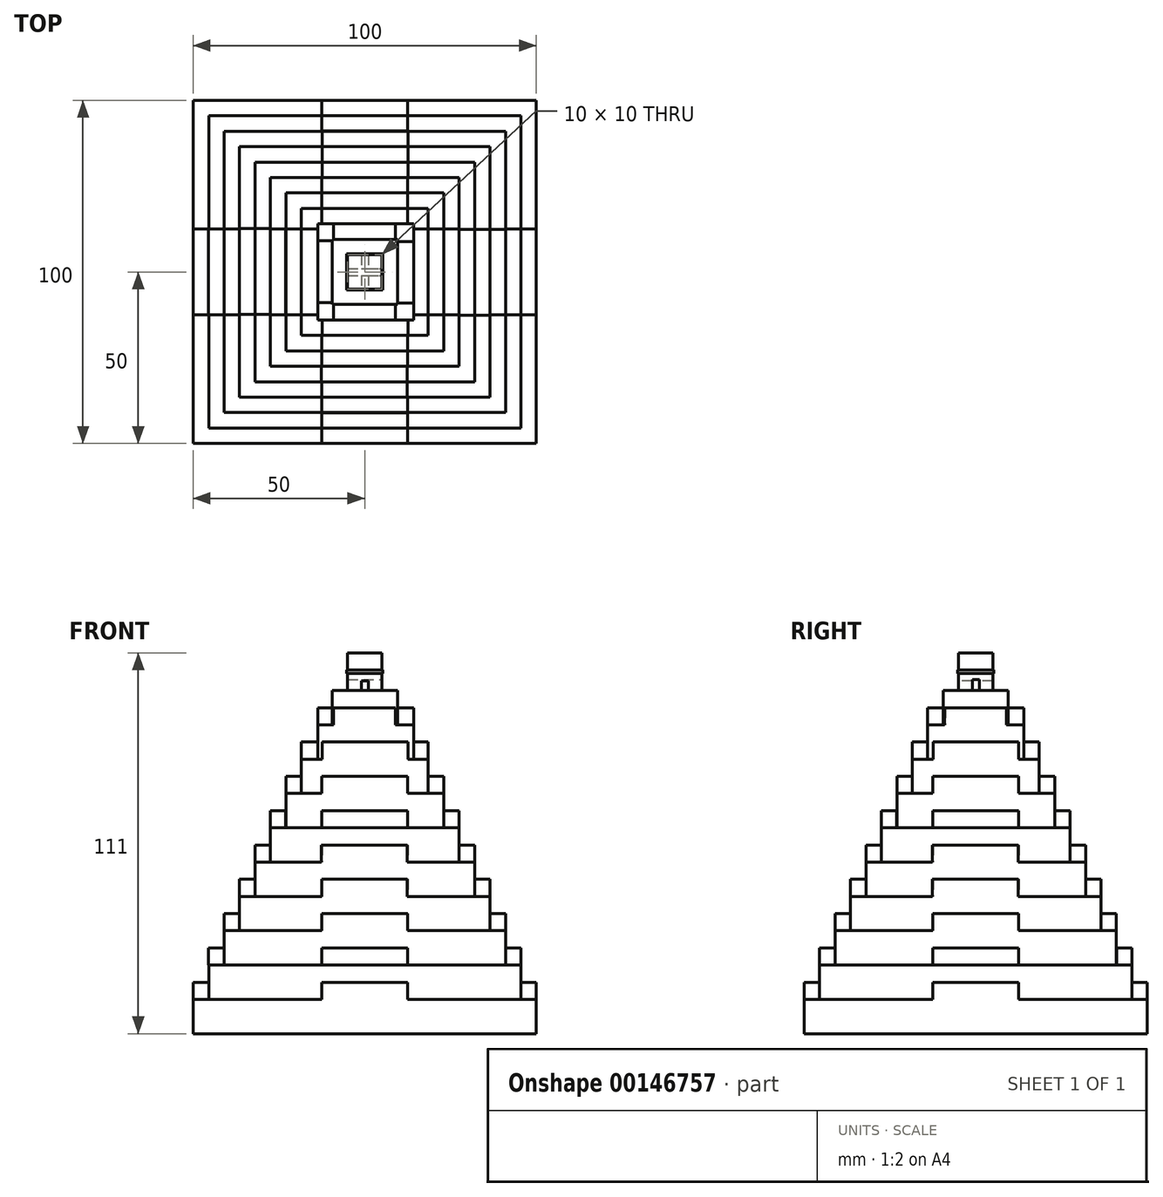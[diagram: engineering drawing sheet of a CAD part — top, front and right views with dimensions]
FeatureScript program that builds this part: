
annotation { "Feature Type Name" : "Feature", "Feature Type Description" : "" }
export const myFeature = defineFeature(function(context is Context, id is Id, definition is map)
    precondition{}
    {
        {
            var Q0;
            Q0=qCreatedBy(makeId("Top.planeOp"),FACE);
            var sketch = newSketch(context, id + "F0", { "sketchPlane" : qUnion([Q0])});
            skLineSegment(sketch, "E0.bottom", {"start": v(-50, 50) * mm, "end": v(50, 50) * mm});
            skLineSegment(sketch, "E0.top", {"start": v(-50, -50) * mm, "end": v(50, -50) * mm});
            skLineSegment(sketch, "E0.left", {"start": v(-50, 50) * mm, "end": v(-50, -50) * mm});
            skLineSegment(sketch, "E0.right", {"start": v(50, 50) * mm, "end": v(50, -50) * mm});
            skPoint(sketch, "E0.middle", {"position": v(0, 0) * mm});
            skSolve(sketch);
        }
        {
            var Q0;
            Q0=makeQuery(id+"F0.imprint","IMPRINT",FACE,{"disambiguationData":[TD([[makeQuery(id+"F0.imprint","IMPRINT",EDGE,{"derivedFrom":sQuery(id+"F0.wireOp",EDGE,"E0.bottom")}),-1.0]])]});
            extrude(context, id + "F1", {"entities" : qUnion([Q0]), "depth" : 10 * mm});
        }
        {
            var Q0;
            Q0=makeQuery(id+"F1.opExtrude","CAP_FACE",FACE,{"disambiguationData":[OSD([sQuery(id+"F0.wireOp",EDGE,"E0.bottom"),sQuery(id+"F0.wireOp",EDGE,"E0.top"),sQuery(id+"F0.wireOp",EDGE,"E0.left"),sQuery(id+"F0.wireOp",EDGE,"E0.right")])],"isStart":false});
            var sketch = newSketch(context, id + "F2", { "sketchPlane" : qUnion([Q0])});
            skLineSegment(sketch, "E1.0", {"start": v(41, 41) * mm, "end": v(-41, 41) * mm});
            skLineSegment(sketch, "E1.1", {"start": v(41, -41) * mm, "end": v(41, 41) * mm});
            skLineSegment(sketch, "E1.2", {"start": v(-41, -41) * mm, "end": v(41, -41) * mm});
            skLineSegment(sketch, "E1.3", {"start": v(-41, 41) * mm, "end": v(-41, -41) * mm});
            skSolve(sketch);
        }
        {
            var Q0;
            Q0 = qSketchRegion(id + "F2", true);
            extrude(context, id + "F3", {"entities" : qUnion([Q0]), "operationType" : NewBodyOperationType.ADD, "depth" : 10 * mm});
        }
        {
            var Q0;
            Q0=makeQuery(id+"F3.opExtrude","CAP_FACE",FACE,{"disambiguationData":[OSD([sQuery(id+"F2.wireOp",EDGE,"E1.0"),sQuery(id+"F2.wireOp",EDGE,"E1.1"),sQuery(id+"F2.wireOp",EDGE,"E1.2"),sQuery(id+"F2.wireOp",EDGE,"E1.3")])],"isStart":false});
            var sketch = newSketch(context, id + "F4", { "sketchPlane" : qUnion([Q0])});
            skLineSegment(sketch, "E2.0", {"start": v(32, -32) * mm, "end": v(32, 32) * mm});
            skLineSegment(sketch, "E2.1", {"start": v(-32, -32) * mm, "end": v(32, -32) * mm});
            skLineSegment(sketch, "E2.2", {"start": v(-32, 32) * mm, "end": v(-32, -32) * mm});
            skLineSegment(sketch, "E2.3", {"start": v(32, 32) * mm, "end": v(-32, 32) * mm});
            skSolve(sketch);
        }
        {
            var Q0;
            Q0 = qSketchRegion(id + "F4", true);
            extrude(context, id + "F5", {"entities" : qUnion([Q0]), "operationType" : NewBodyOperationType.ADD, "depth" : 10 * mm});
        }
        {
            var Q0;
            Q0=makeQuery(id+"F5.opExtrude","CAP_FACE",FACE,{"disambiguationData":[OSD([sQuery(id+"F4.wireOp",EDGE,"E2.0"),sQuery(id+"F4.wireOp",EDGE,"E2.1"),sQuery(id+"F4.wireOp",EDGE,"E2.2"),sQuery(id+"F4.wireOp",EDGE,"E2.3")])],"isStart":false});
            var sketch = newSketch(context, id + "F6", { "sketchPlane" : qUnion([Q0])});
            skLineSegment(sketch, "E3.0", {"start": v(-23, -23) * mm, "end": v(23, -23) * mm});
            skLineSegment(sketch, "E3.1", {"start": v(-23, 23) * mm, "end": v(-23, -23) * mm});
            skLineSegment(sketch, "E3.2", {"start": v(23, 23) * mm, "end": v(-23, 23) * mm});
            skLineSegment(sketch, "E3.3", {"start": v(23, -23) * mm, "end": v(23, 23) * mm});
            skSolve(sketch);
        }
        {
            var Q0;
            Q0 = qSketchRegion(id + "F6", true);
            extrude(context, id + "F7", {"entities" : qUnion([Q0]), "operationType" : NewBodyOperationType.ADD, "depth" : 10 * mm});
        }
        {
            var Q0;
            Q0=makeQuery(id+"F1.opExtrude","CAP_FACE",FACE,{"disambiguationData":[OSD([sQuery(id+"F0.wireOp",EDGE,"E0.bottom"),sQuery(id+"F0.wireOp",EDGE,"E0.top"),sQuery(id+"F0.wireOp",EDGE,"E0.left"),sQuery(id+"F0.wireOp",EDGE,"E0.right")])],"isStart":false});
            var sketch = newSketch(context, id + "F8", { "sketchPlane" : qUnion([Q0])});
            skLineSegment(sketch, "E4.0", {"start": v(45.5, 45.5) * mm, "end": v(-45.5, 45.5) * mm});
            skLineSegment(sketch, "E4.1", {"start": v(45.5, -45.5) * mm, "end": v(45.5, 45.5) * mm});
            skLineSegment(sketch, "E4.2", {"start": v(-45.5, -45.5) * mm, "end": v(45.5, -45.5) * mm});
            skLineSegment(sketch, "E4.3", {"start": v(-45.5, 45.5) * mm, "end": v(-45.5, -45.5) * mm});
            skSolve(sketch);
        }
        {
            var Q0;
            Q0 = qSketchRegion(id + "F8", true);
            extrude(context, id + "F9", {"entities" : qUnion([Q0]), "operationType" : NewBodyOperationType.ADD, "depth" : 10 * mm});
        }
        {
            var Q0;
            Q0=makeQuery(id+"F9.boolean.opBoolean","MERGE",FACE,{"derivedFrom":[makeQuery(id+"F3.opExtrude","CAP_FACE",FACE,{"disambiguationData":[OSD([sQuery(id+"F2.wireOp",EDGE,"E1.0"),sQuery(id+"F2.wireOp",EDGE,"E1.1"),sQuery(id+"F2.wireOp",EDGE,"E1.2"),sQuery(id+"F2.wireOp",EDGE,"E1.3")])],"isStart":false}),makeQuery(id+"F9.opExtrude","CAP_FACE",FACE,{"disambiguationData":[OSD([sQuery(id+"F8.wireOp",EDGE,"E4.0"),sQuery(id+"F8.wireOp",EDGE,"E4.1"),sQuery(id+"F8.wireOp",EDGE,"E4.2"),sQuery(id+"F8.wireOp",EDGE,"E4.3")])],"isStart":false})]});
            var sketch = newSketch(context, id + "F10", { "sketchPlane" : qUnion([Q0])});
            skLineSegment(sketch, "E5.0", {"start": v(41, -41) * mm, "end": v(41, 41) * mm});
            skLineSegment(sketch, "E5.1", {"start": v(-41, -41) * mm, "end": v(41, -41) * mm});
            skLineSegment(sketch, "E5.2", {"start": v(-41, 41) * mm, "end": v(-41, -41) * mm});
            skLineSegment(sketch, "E5.3", {"start": v(41, 41) * mm, "end": v(-41, 41) * mm});
            skSolve(sketch);
        }
        {
            var Q0;
            Q0 = qSketchRegion(id + "F10", true);
            extrude(context, id + "F11", {"entities" : qUnion([Q0]), "operationType" : NewBodyOperationType.ADD, "depth" : 10 * mm});
        }
        {
            var Q0;
            Q0=makeQuery(id+"F11.boolean.opBoolean","MERGE",FACE,{"derivedFrom":[makeQuery(id+"F5.opExtrude","CAP_FACE",FACE,{"disambiguationData":[OSD([sQuery(id+"F4.wireOp",EDGE,"E2.0"),sQuery(id+"F4.wireOp",EDGE,"E2.1"),sQuery(id+"F4.wireOp",EDGE,"E2.2"),sQuery(id+"F4.wireOp",EDGE,"E2.3")])],"isStart":false}),makeQuery(id+"F11.opExtrude","CAP_FACE",FACE,{"disambiguationData":[OSD([sQuery(id+"F10.wireOp",EDGE,"E5.0"),sQuery(id+"F10.wireOp",EDGE,"E5.1"),sQuery(id+"F10.wireOp",EDGE,"E5.2"),sQuery(id+"F10.wireOp",EDGE,"E5.3")])],"isStart":false})]});
            var sketch = newSketch(context, id + "F12", { "sketchPlane" : qUnion([Q0])});
            skLineSegment(sketch, "E6.0", {"start": v(-36.5, -36.5) * mm, "end": v(36.5, -36.5) * mm});
            skLineSegment(sketch, "E6.1", {"start": v(-36.5, 36.5) * mm, "end": v(-36.5, -36.5) * mm});
            skLineSegment(sketch, "E6.2", {"start": v(36.5, 36.5) * mm, "end": v(-36.5, 36.5) * mm});
            skLineSegment(sketch, "E6.3", {"start": v(36.5, -36.5) * mm, "end": v(36.5, 36.5) * mm});
            skSolve(sketch);
        }
        {
            var Q0;
            Q0 = qSketchRegion(id + "F12", true);
            extrude(context, id + "F13", {"entities" : qUnion([Q0]), "operationType" : NewBodyOperationType.ADD, "depth" : 10 * mm});
        }
        {
            var Q0;
            Q0=makeQuery(id+"F13.boolean.opBoolean","MERGE",FACE,{"derivedFrom":[makeQuery(id+"F7.opExtrude","CAP_FACE",FACE,{"disambiguationData":[OSD([sQuery(id+"F6.wireOp",EDGE,"E3.0"),sQuery(id+"F6.wireOp",EDGE,"E3.1"),sQuery(id+"F6.wireOp",EDGE,"E3.2"),sQuery(id+"F6.wireOp",EDGE,"E3.3")])],"isStart":false}),makeQuery(id+"F13.opExtrude","CAP_FACE",FACE,{"disambiguationData":[OSD([sQuery(id+"F12.wireOp",EDGE,"E6.0"),sQuery(id+"F12.wireOp",EDGE,"E6.1"),sQuery(id+"F12.wireOp",EDGE,"E6.2"),sQuery(id+"F12.wireOp",EDGE,"E6.3")])],"isStart":false})]});
            var sketch = newSketch(context, id + "F14", { "sketchPlane" : qUnion([Q0])});
            skLineSegment(sketch, "E7.0", {"start": v(-32, 32) * mm, "end": v(-32, -32) * mm});
            skLineSegment(sketch, "E7.1", {"start": v(32, 32) * mm, "end": v(-32, 32) * mm});
            skLineSegment(sketch, "E7.2", {"start": v(32, -32) * mm, "end": v(32, 32) * mm});
            skLineSegment(sketch, "E7.3", {"start": v(-32, -32) * mm, "end": v(32, -32) * mm});
            skSolve(sketch);
        }
        {
            var Q0;
            Q0 = qSketchRegion(id + "F14", true);
            extrude(context, id + "F15", {"entities" : qUnion([Q0]), "operationType" : NewBodyOperationType.ADD, "depth" : 10 * mm});
        }
        {
            var Q0;
            Q0=makeQuery(id+"F15.opExtrude","CAP_FACE",FACE,{"disambiguationData":[OSD([sQuery(id+"F14.wireOp",EDGE,"E7.0"),sQuery(id+"F14.wireOp",EDGE,"E7.1"),sQuery(id+"F14.wireOp",EDGE,"E7.2"),sQuery(id+"F14.wireOp",EDGE,"E7.3")])],"isStart":false});
            var sketch = newSketch(context, id + "F16", { "sketchPlane" : qUnion([Q0])});
            skLineSegment(sketch, "E8.0", {"start": v(27.5, 27.5) * mm, "end": v(-27.5, 27.5) * mm});
            skLineSegment(sketch, "E8.1", {"start": v(27.5, -27.5) * mm, "end": v(27.5, 27.5) * mm});
            skLineSegment(sketch, "E8.2", {"start": v(-27.5, -27.5) * mm, "end": v(27.5, -27.5) * mm});
            skLineSegment(sketch, "E8.3", {"start": v(-27.5, 27.5) * mm, "end": v(-27.5, -27.5) * mm});
            skSolve(sketch);
        }
        {
            var Q0;
            Q0 = qSketchRegion(id + "F16", true);
            extrude(context, id + "F17", {"entities" : qUnion([Q0]), "operationType" : NewBodyOperationType.ADD, "depth" : 10 * mm});
        }
        {
            var Q0;
            Q0=makeQuery(id+"F17.opExtrude","CAP_FACE",FACE,{"disambiguationData":[OSD([sQuery(id+"F16.wireOp",EDGE,"E8.0"),sQuery(id+"F16.wireOp",EDGE,"E8.1"),sQuery(id+"F16.wireOp",EDGE,"E8.2"),sQuery(id+"F16.wireOp",EDGE,"E8.3")])],"isStart":false});
            var sketch = newSketch(context, id + "F18", { "sketchPlane" : qUnion([Q0])});
            skLineSegment(sketch, "E9.0", {"start": v(23, -23) * mm, "end": v(23, 23) * mm});
            skLineSegment(sketch, "E9.1", {"start": v(-23, -23) * mm, "end": v(23, -23) * mm});
            skLineSegment(sketch, "E9.2", {"start": v(-23, 23) * mm, "end": v(-23, -23) * mm});
            skLineSegment(sketch, "E9.3", {"start": v(23, 23) * mm, "end": v(-23, 23) * mm});
            skLineSegment(sketch, "E10.0", {"start": v(32.5, -32.5) * mm, "end": v(32.5, 32.5) * mm});
            skLineSegment(sketch, "E10.1", {"start": v(-32.5, -32.5) * mm, "end": v(32.5, -32.5) * mm});
            skLineSegment(sketch, "E10.2", {"start": v(-32.5, 32.5) * mm, "end": v(-32.5, -32.5) * mm});
            skLineSegment(sketch, "E10.3", {"start": v(32.5, 32.5) * mm, "end": v(-32.5, 32.5) * mm});
            skSolve(sketch);
        }
        {
            var Q0;
            Q0=makeQuery(id+"F18.imprint","IMPRINT",FACE,{"disambiguationData":[TD([[makeQuery(id+"F18.imprint","IMPRINT",EDGE,{"derivedFrom":sQuery(id+"F18.wireOp",EDGE,"E9.0")}),-1.0]])]});
            var sketch = newSketch(context, id + "F19", { "sketchPlane" : qUnion([Q0])});
            skLineSegment(sketch, "E11.bottom", {"start": v(-23, 23) * mm, "end": v(23, 23) * mm});
            skLineSegment(sketch, "E11.top", {"start": v(-23, -23) * mm, "end": v(23, -23) * mm});
            skLineSegment(sketch, "E11.left", {"start": v(-23, 23) * mm, "end": v(-23, -23) * mm});
            skLineSegment(sketch, "E11.right", {"start": v(23, 23) * mm, "end": v(23, -23) * mm});
            skPoint(sketch, "E11.middle", {"position": v(0, 0) * mm});
            skSolve(sketch);
        }
        {
            var Q0;
            Q0 = qSketchRegion(id + "F19", true);
            extrude(context, id + "F20", {"entities" : qUnion([Q0]), "operationType" : NewBodyOperationType.ADD, "depth" : 10 * mm});
        }
        {
            var Q0;
            Q0=makeQuery(id+"F20.opExtrude","CAP_FACE",FACE,{"disambiguationData":[OSD([sQuery(id+"F19.wireOp",EDGE,"E11.bottom"),sQuery(id+"F19.wireOp",EDGE,"E11.top"),sQuery(id+"F19.wireOp",EDGE,"E11.left"),sQuery(id+"F19.wireOp",EDGE,"E11.right")])],"isStart":false});
            var sketch = newSketch(context, id + "F21", { "sketchPlane" : qUnion([Q0])});
            skLineSegment(sketch, "E12.bottom", {"start": v(-18.5, 18.5) * mm, "end": v(18.5, 18.5) * mm});
            skLineSegment(sketch, "E12.top", {"start": v(-18.5, -18.5) * mm, "end": v(18.5, -18.5) * mm});
            skLineSegment(sketch, "E12.left", {"start": v(-18.5, 18.5) * mm, "end": v(-18.5, -18.5) * mm});
            skLineSegment(sketch, "E12.right", {"start": v(18.5, 18.5) * mm, "end": v(18.5, -18.5) * mm});
            skPoint(sketch, "E12.middle", {"position": v(0, 0) * mm});
            skSolve(sketch);
        }
        {
            var Q0;
            Q0 = qSketchRegion(id + "F21", true);
            extrude(context, id + "F22", {"entities" : qUnion([Q0]), "operationType" : NewBodyOperationType.ADD, "depth" : 10 * mm});
        }
        {
            var Q0;
            Q0=makeQuery(id+"F22.opExtrude","CAP_FACE",FACE,{"disambiguationData":[OSD([sQuery(id+"F21.wireOp",EDGE,"E12.bottom"),sQuery(id+"F21.wireOp",EDGE,"E12.top"),sQuery(id+"F21.wireOp",EDGE,"E12.left"),sQuery(id+"F21.wireOp",EDGE,"E12.right")])],"isStart":false});
            var sketch = newSketch(context, id + "F23", { "sketchPlane" : qUnion([Q0])});
            skLineSegment(sketch, "E13.bottom", {"start": v(-13.7, 14) * mm, "end": v(14.3, 14) * mm});
            skLineSegment(sketch, "E13.top", {"start": v(-13.7, -14) * mm, "end": v(14.3, -14) * mm});
            skLineSegment(sketch, "E13.left", {"start": v(-13.7, 14) * mm, "end": v(-13.7, -14) * mm});
            skLineSegment(sketch, "E13.right", {"start": v(14.3, 14) * mm, "end": v(14.3, -14) * mm});
            skPoint(sketch, "E13.middle", {"position": v(0.3, 0) * mm});
            skSolve(sketch);
        }
        {
            var Q0;
            Q0 = qSketchRegion(id + "F23", true);
            extrude(context, id + "F24", {"entities" : qUnion([Q0]), "operationType" : NewBodyOperationType.ADD, "depth" : 10 * mm});
        }
        {
            var Q0;
            Q0=makeQuery(id+"F24.opExtrude","CAP_FACE",FACE,{"disambiguationData":[OSD([sQuery(id+"F23.wireOp",EDGE,"E13.bottom"),sQuery(id+"F23.wireOp",EDGE,"E13.top"),sQuery(id+"F23.wireOp",EDGE,"E13.left"),sQuery(id+"F23.wireOp",EDGE,"E13.right")])],"isStart":false});
            var sketch = newSketch(context, id + "F25", { "sketchPlane" : qUnion([Q0])});
            skLineSegment(sketch, "E14.bottom", {"start": v(-9.5, 9.5) * mm, "end": v(9.5, 9.5) * mm});
            skLineSegment(sketch, "E14.top", {"start": v(-9.5, -9.5) * mm, "end": v(9.5, -9.5) * mm});
            skLineSegment(sketch, "E14.left", {"start": v(-9.5, 9.5) * mm, "end": v(-9.5, -9.5) * mm});
            skLineSegment(sketch, "E14.right", {"start": v(9.5, 9.5) * mm, "end": v(9.5, -9.5) * mm});
            skPoint(sketch, "E14.middle", {"position": v(0, 0) * mm});
            skSolve(sketch);
        }
        {
            var Q0;
            Q0 = qSketchRegion(id + "F25", true);
            extrude(context, id + "F26", {"entities" : qUnion([Q0]), "operationType" : NewBodyOperationType.ADD, "depth" : 10 * mm});
        }
        {
            var Q0;
            Q0=makeQuery(id+"F26.opExtrude","CAP_FACE",FACE,{"disambiguationData":[OSD([sQuery(id+"F25.wireOp",EDGE,"E14.bottom"),sQuery(id+"F25.wireOp",EDGE,"E14.top"),sQuery(id+"F25.wireOp",EDGE,"E14.left"),sQuery(id+"F25.wireOp",EDGE,"E14.right")])],"isStart":false});
            var sketch = newSketch(context, id + "F27", { "sketchPlane" : qUnion([Q0])});
            skLineSegment(sketch, "E15.bottom", {"start": v(-5, 5) * mm, "end": v(5, 5) * mm});
            skLineSegment(sketch, "E15.top", {"start": v(-5, -5) * mm, "end": v(5, -5) * mm});
            skLineSegment(sketch, "E15.left", {"start": v(-5, 5) * mm, "end": v(-5, -5) * mm});
            skLineSegment(sketch, "E15.right", {"start": v(5, 5) * mm, "end": v(5, -5) * mm});
            skPoint(sketch, "E15.middle", {"position": v(0, 0) * mm});
            skSolve(sketch);
        }
        {
            var Q0;
            Q0 = qSketchRegion(id + "F27", true);
            extrude(context, id + "F28", {"entities" : qUnion([Q0]), "operationType" : NewBodyOperationType.ADD, "depth" : 5 * mm});
        }
        {
            var Q0;
            Q0=makeQuery(id+"F28.opExtrude","CAP_FACE",FACE,{"disambiguationData":[OSD([sQuery(id+"F27.wireOp",EDGE,"E15.bottom"),sQuery(id+"F27.wireOp",EDGE,"E15.top"),sQuery(id+"F27.wireOp",EDGE,"E15.left"),sQuery(id+"F27.wireOp",EDGE,"E15.right")])],"isStart":false});
            var sketch = newSketch(context, id + "F29", { "sketchPlane" : qUnion([Q0])});
            skLineSegment(sketch, "E16.bottom", {"start": v(-5.25, 5.25) * mm, "end": v(5.25, 5.25) * mm});
            skLineSegment(sketch, "E16.top", {"start": v(-5.25, -5.25) * mm, "end": v(5.25, -5.25) * mm});
            skLineSegment(sketch, "E16.left", {"start": v(-5.25, 5.25) * mm, "end": v(-5.25, -5.25) * mm});
            skLineSegment(sketch, "E16.right", {"start": v(5.25, 5.25) * mm, "end": v(5.25, -5.25) * mm});
            skPoint(sketch, "E16.middle", {"position": v(0, 0) * mm});
            skSolve(sketch);
        }
        {
            var Q0;
            Q0 = qSketchRegion(id + "F29", true);
            extrude(context, id + "F30", {"entities" : qUnion([Q0]), "operationType" : NewBodyOperationType.ADD, "depth" : 1 * mm});
        }
        {
            var Q0;
            Q0=makeQuery(id+"F30.opExtrude","CAP_FACE",FACE,{"disambiguationData":[OSD([sQuery(id+"F29.wireOp",EDGE,"E16.bottom"),sQuery(id+"F29.wireOp",EDGE,"E16.top"),sQuery(id+"F29.wireOp",EDGE,"E16.left"),sQuery(id+"F29.wireOp",EDGE,"E16.right")])],"isStart":false});
            var sketch = newSketch(context, id + "F31", { "sketchPlane" : qUnion([Q0])});
            skLineSegment(sketch, "E17.bottom", {"start": v(-5, 5) * mm, "end": v(5, 5) * mm});
            skLineSegment(sketch, "E17.top", {"start": v(-5, -5) * mm, "end": v(5, -5) * mm});
            skLineSegment(sketch, "E17.left", {"start": v(-5, 5) * mm, "end": v(-5, -5) * mm});
            skLineSegment(sketch, "E17.right", {"start": v(5, 5) * mm, "end": v(5, -5) * mm});
            skPoint(sketch, "E17.middle", {"position": v(0, 0) * mm});
            skSolve(sketch);
        }
        {
            var Q0;
            Q0 = qSketchRegion(id + "F31", true);
            extrude(context, id + "F32", {"entities" : qUnion([Q0]), "operationType" : NewBodyOperationType.ADD, "depth" : 5 * mm});
        }
        {
            var Q0;
            Q0=makeQuery(id+"F28.opExtrude","SWEPT_FACE",FACE,{"disambiguationData":[OSD([sQuery(id+"F27.wireOp",EDGE,"E15.top")])]});
            var sketch = newSketch(context, id + "F33", { "sketchPlane" : qUnion([Q0])});
            skLineSegment(sketch, "E18.bottom", {"start": v(-0.98, 100) * mm, "end": v(0.98, 100) * mm});
            skLineSegment(sketch, "E18.top", {"start": v(-0.98, 102.81) * mm, "end": v(0.98, 102.81) * mm});
            skLineSegment(sketch, "E18.left", {"start": v(-0.98, 100) * mm, "end": v(-0.98, 102.81) * mm});
            skLineSegment(sketch, "E18.right", {"start": v(0.98, 100) * mm, "end": v(0.98, 102.81) * mm});
            skPoint(sketch, "E18.middle", {"position": v(0, 101.4) * mm});
            skSolve(sketch);
        }
        {
            var Q0;
            Q0 = qSketchRegion(id + "F33", true);
            extrude(context, id + "F34", {"entities" : qUnion([Q0]), "operationType" : NewBodyOperationType.REMOVE, "oppositeDirection" : true, "depth" : 25 * mm});
        }
        {
            var Q0;
            Q0=makeQuery(id+"F28.opExtrude","SWEPT_FACE",FACE,{"disambiguationData":[OSD([sQuery(id+"F27.wireOp",EDGE,"E15.right")])]});
            var sketch = newSketch(context, id + "F35", { "sketchPlane" : qUnion([Q0])});
            skLineSegment(sketch, "E19.bottom", {"start": v(-1.01, 100) * mm, "end": v(1.01, 100) * mm});
            skLineSegment(sketch, "E19.top", {"start": v(-1.01, 103.22) * mm, "end": v(1.01, 103.22) * mm});
            skLineSegment(sketch, "E19.left", {"start": v(-1.01, 100) * mm, "end": v(-1.01, 103.22) * mm});
            skLineSegment(sketch, "E19.right", {"start": v(1.01, 100) * mm, "end": v(1.01, 103.22) * mm});
            skPoint(sketch, "E19.middle", {"position": v(0, 101.6) * mm});
            skSolve(sketch);
        }
        {
            var Q0;
            Q0 = qSketchRegion(id + "F35", true);
            extrude(context, id + "F36", {"entities" : qUnion([Q0]), "operationType" : NewBodyOperationType.REMOVE, "oppositeDirection" : true, "depth" : 25 * mm});
        }
        {
            var Q0;
            Q0=makeQuery(id+"F1.opExtrude","CAP_FACE",FACE,{"disambiguationData":[OSD([sQuery(id+"F0.wireOp",EDGE,"E0.bottom"),sQuery(id+"F0.wireOp",EDGE,"E0.top"),sQuery(id+"F0.wireOp",EDGE,"E0.left"),sQuery(id+"F0.wireOp",EDGE,"E0.right")])],"isStart":false});
            var sketch = newSketch(context, id + "F37", { "sketchPlane" : qUnion([Q0])});
            skLineSegment(sketch, "E20.bottom", {"start": v(0, 50) * mm, "end": v(12.5, 50) * mm});
            skLineSegment(sketch, "E20.top", {"start": v(0, 45.5) * mm, "end": v(12.5, 45.5) * mm});
            skLineSegment(sketch, "E20.left", {"start": v(0, 50) * mm, "end": v(0, 45.5) * mm});
            skLineSegment(sketch, "E20.right", {"start": v(12.5, 50) * mm, "end": v(12.5, 45.5) * mm});
            skLineSegment(sketch, "E21", {"start": v(0, -56.15) * mm, "end": v(0, 57.62) * mm});
            skLineSegment(sketch, "E22", {"start": v(-72.6, 0) * mm, "end": v(68.28, 0) * mm});
            skPoint(sketch, "E22.endSnap0", {"position": v(50, 0) * mm});
            skLineSegment(sketch, "E23.MirrorCS", {"start": v(0, 50) * mm, "end": v(-12.5, 50) * mm});
            skLineSegment(sketch, "E24.MirrorCS", {"start": v(0, 45.5) * mm, "end": v(-12.5, 45.5) * mm});
            skLineSegment(sketch, "E25.MirrorCS", {"start": v(-12.5, 50) * mm, "end": v(-12.5, 45.5) * mm});
            skLineSegment(sketch, "E26.MirrorCS", {"start": v(0, -45.5) * mm, "end": v(-12.5, -45.5) * mm});
            skLineSegment(sketch, "E27.MirrorCS", {"start": v(0, -50) * mm, "end": v(-12.5, -50) * mm});
            skLineSegment(sketch, "E28.MirrorCS", {"start": v(-12.5, -50) * mm, "end": v(-12.5, -45.5) * mm});
            skLineSegment(sketch, "E29.MirrorCS", {"start": v(0, -45.5) * mm, "end": v(12.5, -45.5) * mm});
            skLineSegment(sketch, "E30.MirrorCS", {"start": v(0, -50) * mm, "end": v(12.5, -50) * mm});
            skLineSegment(sketch, "E31.MirrorCS", {"start": v(12.5, -50) * mm, "end": v(12.5, -45.5) * mm});
            skLineSegment(sketch, "E32.1.0", {"start": v(50, 0) * mm, "end": v(50, 12.5) * mm});
            skLineSegment(sketch, "E32.1.1", {"start": v(45.5, 0) * mm, "end": v(45.5, 12.5) * mm});
            skLineSegment(sketch, "E32.1.2", {"start": v(50, 12.5) * mm, "end": v(45.5, 12.5) * mm});
            skLineSegment(sketch, "E32.1.3", {"start": v(45.5, 0) * mm, "end": v(45.5, -12.5) * mm});
            skLineSegment(sketch, "E32.1.4", {"start": v(50, 0) * mm, "end": v(50, -12.5) * mm});
            skLineSegment(sketch, "E32.1.5", {"start": v(50, -12.5) * mm, "end": v(45.5, -12.5) * mm});
            skLineSegment(sketch, "E32.3.0", {"start": v(-50, 0) * mm, "end": v(-50, -12.5) * mm});
            skLineSegment(sketch, "E32.3.1", {"start": v(-45.5, 0) * mm, "end": v(-45.5, -12.5) * mm});
            skLineSegment(sketch, "E32.3.2", {"start": v(-50, -12.5) * mm, "end": v(-45.5, -12.5) * mm});
            skLineSegment(sketch, "E32.3.3", {"start": v(-45.5, 0) * mm, "end": v(-45.5, 12.5) * mm});
            skLineSegment(sketch, "E32.3.4", {"start": v(-50, 0) * mm, "end": v(-50, 12.5) * mm});
            skLineSegment(sketch, "E32.3.5", {"start": v(-50, 12.5) * mm, "end": v(-45.5, 12.5) * mm});
            skPoint(sketch, "E32.center", {"position": v(0, 0) * mm});
            skLineSegment(sketch, "E32.anchor1", {"start": v(0, 0) * mm, "end": v(-12.5, 50) * mm, "construction": true});
            skLineSegment(sketch, "E32.anchor2", {"start": v(0, 0) * mm, "end": v(-50, -12.5) * mm, "construction": true});
            skSolve(sketch);
        }
        {
            var Q0;
            Q0 = qSketchRegion(id + "F37", true);
            extrude(context, id + "F38", {"entities" : qUnion([Q0]), "operationType" : NewBodyOperationType.ADD, "depth" : 5 * mm});
        }
        {
            var Q0;
            Q0=makeQuery(id+"F9.boolean.opBoolean","MERGE",FACE,{"derivedFrom":[makeQuery(id+"F3.opExtrude","CAP_FACE",FACE,{"disambiguationData":[OSD([sQuery(id+"F2.wireOp",EDGE,"E1.0"),sQuery(id+"F2.wireOp",EDGE,"E1.1"),sQuery(id+"F2.wireOp",EDGE,"E1.2"),sQuery(id+"F2.wireOp",EDGE,"E1.3")])],"isStart":false}),makeQuery(id+"F9.opExtrude","CAP_FACE",FACE,{"disambiguationData":[OSD([sQuery(id+"F8.wireOp",EDGE,"E4.0"),sQuery(id+"F8.wireOp",EDGE,"E4.1"),sQuery(id+"F8.wireOp",EDGE,"E4.2"),sQuery(id+"F8.wireOp",EDGE,"E4.3")])],"isStart":false})]});
            var sketch = newSketch(context, id + "F39", { "sketchPlane" : qUnion([Q0])});
            skLineSegment(sketch, "E33.bottom", {"start": v(-12.45, 45.5) * mm, "end": v(12.43, 45.5) * mm});
            skLineSegment(sketch, "E33.top", {"start": v(-12.45, 41.51) * mm, "end": v(12.43, 41.51) * mm});
            skLineSegment(sketch, "E33.left", {"start": v(-12.45, 45.5) * mm, "end": v(-12.45, 41.51) * mm});
            skLineSegment(sketch, "E33.right", {"start": v(12.43, 45.5) * mm, "end": v(12.43, 41.51) * mm});
            skSolve(sketch);
        }
        {
            var Q0;
            Q0=makeQuery(id+"F39.imprint","IMPRINT",FACE,{"disambiguationData":[TD([[makeQuery(id+"F39.imprint","IMPRINT",EDGE,{"derivedFrom":sQuery(id+"F39.wireOp",EDGE,"E33.top")}),-1.0]])]});
            var sketch = newSketch(context, id + "F40", { "sketchPlane" : qUnion([Q0])});
            skLineSegment(sketch, "E34.bottom", {"start": v(-12.5, 45.54) * mm, "end": v(12.5, 45.54) * mm});
            skLineSegment(sketch, "E34.top", {"start": v(-12.5, 41.04) * mm, "end": v(12.5, 41.04) * mm});
            skLineSegment(sketch, "E34.left", {"start": v(-12.5, 45.54) * mm, "end": v(-12.5, 41.04) * mm});
            skLineSegment(sketch, "E34.right", {"start": v(12.5, 45.54) * mm, "end": v(12.5, 41.04) * mm});
            skLineSegment(sketch, "E35.1.0", {"start": v(-45.54, -12.5) * mm, "end": v(-45.54, 12.5) * mm});
            skLineSegment(sketch, "E35.1.1", {"start": v(-45.54, -12.5) * mm, "end": v(-41.04, -12.5) * mm});
            skLineSegment(sketch, "E35.1.2", {"start": v(-41.04, -12.5) * mm, "end": v(-41.04, 12.5) * mm});
            skLineSegment(sketch, "E35.1.3", {"start": v(-45.54, 12.5) * mm, "end": v(-41.04, 12.5) * mm});
            skLineSegment(sketch, "E35.2.0", {"start": v(12.5, -45.54) * mm, "end": v(-12.5, -45.54) * mm});
            skLineSegment(sketch, "E35.2.1", {"start": v(12.5, -45.54) * mm, "end": v(12.5, -41.04) * mm});
            skLineSegment(sketch, "E35.2.2", {"start": v(12.5, -41.04) * mm, "end": v(-12.5, -41.04) * mm});
            skLineSegment(sketch, "E35.2.3", {"start": v(-12.5, -45.54) * mm, "end": v(-12.5, -41.04) * mm});
            skLineSegment(sketch, "E35.3.0", {"start": v(45.54, 12.5) * mm, "end": v(45.54, -12.5) * mm});
            skLineSegment(sketch, "E35.3.1", {"start": v(45.54, 12.5) * mm, "end": v(41.04, 12.5) * mm});
            skLineSegment(sketch, "E35.3.2", {"start": v(41.04, 12.5) * mm, "end": v(41.04, -12.5) * mm});
            skLineSegment(sketch, "E35.3.3", {"start": v(45.54, -12.5) * mm, "end": v(41.04, -12.5) * mm});
            skPoint(sketch, "E35.center", {"position": v(0, 0) * mm});
            skSolve(sketch);
        }
        {
            var Q0;
            Q0 = qSketchRegion(id + "F40", true);
            extrude(context, id + "F41", {"entities" : qUnion([Q0]), "operationType" : NewBodyOperationType.ADD, "depth" : 5 * mm});
        }
        {
            var Q0;
            Q0=makeQuery(id+"F11.boolean.opBoolean","MERGE",FACE,{"derivedFrom":[makeQuery(id+"F5.opExtrude","CAP_FACE",FACE,{"disambiguationData":[OSD([sQuery(id+"F4.wireOp",EDGE,"E2.0"),sQuery(id+"F4.wireOp",EDGE,"E2.1"),sQuery(id+"F4.wireOp",EDGE,"E2.2"),sQuery(id+"F4.wireOp",EDGE,"E2.3")])],"isStart":false}),makeQuery(id+"F11.opExtrude","CAP_FACE",FACE,{"disambiguationData":[OSD([sQuery(id+"F10.wireOp",EDGE,"E5.0"),sQuery(id+"F10.wireOp",EDGE,"E5.1"),sQuery(id+"F10.wireOp",EDGE,"E5.2"),sQuery(id+"F10.wireOp",EDGE,"E5.3")])],"isStart":false})]});
            var sketch = newSketch(context, id + "F42", { "sketchPlane" : qUnion([Q0])});
            skLineSegment(sketch, "E36.bottom", {"start": v(-12.45, 41) * mm, "end": v(12.55, 41) * mm});
            skLineSegment(sketch, "E36.top", {"start": v(-12.45, 36.5) * mm, "end": v(12.55, 36.5) * mm});
            skLineSegment(sketch, "E36.left", {"start": v(-12.45, 41) * mm, "end": v(-12.45, 36.5) * mm});
            skLineSegment(sketch, "E36.right", {"start": v(12.55, 41) * mm, "end": v(12.55, 36.5) * mm});
            skLineSegment(sketch, "E37.1.0", {"start": v(-41, -12.45) * mm, "end": v(-36.5, -12.45) * mm});
            skLineSegment(sketch, "E37.1.1", {"start": v(-41, -12.45) * mm, "end": v(-41, 12.55) * mm});
            skLineSegment(sketch, "E37.2.0", {"start": v(12.45, -41) * mm, "end": v(12.45, -36.5) * mm});
            skLineSegment(sketch, "E37.2.1", {"start": v(12.45, -41) * mm, "end": v(-12.55, -41) * mm});
            skPoint(sketch, "E37.center", {"position": v(0, 0) * mm});
            skLineSegment(sketch, "E38.2.3.0", {"start": v(41, 12.45) * mm, "end": v(36.5, 12.45) * mm});
            skLineSegment(sketch, "E38.3.3.0", {"start": v(41, 12.45) * mm, "end": v(41, -12.55) * mm});
            skLineSegment(sketch, "E39.1.0", {"start": v(-36.5, -12.45) * mm, "end": v(-36.5, 12.55) * mm});
            skLineSegment(sketch, "E39.1.1", {"start": v(-41, 12.55) * mm, "end": v(-36.5, 12.55) * mm});
            skLineSegment(sketch, "E39.2.0", {"start": v(12.45, -36.5) * mm, "end": v(-12.55, -36.5) * mm});
            skLineSegment(sketch, "E39.2.1", {"start": v(-12.55, -41) * mm, "end": v(-12.55, -36.5) * mm});
            skLineSegment(sketch, "E39.3.0", {"start": v(36.5, 12.45) * mm, "end": v(36.5, -12.55) * mm});
            skLineSegment(sketch, "E39.3.1", {"start": v(41, -12.55) * mm, "end": v(36.5, -12.55) * mm});
            skSolve(sketch);
        }
        {
            var Q0;
            Q0 = qSketchRegion(id + "F42", true);
            extrude(context, id + "F43", {"entities" : qUnion([Q0]), "operationType" : NewBodyOperationType.ADD, "depth" : 5 * mm});
        }
        {
            var Q0;
            Q0=makeQuery(id+"F13.boolean.opBoolean","MERGE",FACE,{"derivedFrom":[makeQuery(id+"F7.opExtrude","CAP_FACE",FACE,{"disambiguationData":[OSD([sQuery(id+"F6.wireOp",EDGE,"E3.0"),sQuery(id+"F6.wireOp",EDGE,"E3.1"),sQuery(id+"F6.wireOp",EDGE,"E3.2"),sQuery(id+"F6.wireOp",EDGE,"E3.3")])],"isStart":false}),makeQuery(id+"F13.opExtrude","CAP_FACE",FACE,{"disambiguationData":[OSD([sQuery(id+"F12.wireOp",EDGE,"E6.0"),sQuery(id+"F12.wireOp",EDGE,"E6.1"),sQuery(id+"F12.wireOp",EDGE,"E6.2"),sQuery(id+"F12.wireOp",EDGE,"E6.3")])],"isStart":false})]});
            var sketch = newSketch(context, id + "F44", { "sketchPlane" : qUnion([Q0])});
            skLineSegment(sketch, "E40.bottom", {"start": v(-12.4, 36.5) * mm, "end": v(12.6, 36.5) * mm});
            skLineSegment(sketch, "E40.top", {"start": v(-12.4, 32) * mm, "end": v(12.6, 32) * mm});
            skLineSegment(sketch, "E40.left", {"start": v(-12.4, 36.5) * mm, "end": v(-12.4, 32) * mm});
            skLineSegment(sketch, "E40.right", {"start": v(12.6, 36.5) * mm, "end": v(12.6, 32) * mm});
            skLineSegment(sketch, "E41.1.0", {"start": v(-36.5, -12.4) * mm, "end": v(-36.5, 12.6) * mm});
            skLineSegment(sketch, "E41.1.1", {"start": v(-36.5, -12.4) * mm, "end": v(-32, -12.4) * mm});
            skLineSegment(sketch, "E41.1.2", {"start": v(-32, -12.4) * mm, "end": v(-32, 12.6) * mm});
            skLineSegment(sketch, "E41.1.3", {"start": v(-36.5, 12.6) * mm, "end": v(-32, 12.6) * mm});
            skLineSegment(sketch, "E41.2.0", {"start": v(12.4, -36.5) * mm, "end": v(-12.6, -36.5) * mm});
            skLineSegment(sketch, "E41.2.1", {"start": v(12.4, -36.5) * mm, "end": v(12.4, -32) * mm});
            skLineSegment(sketch, "E41.2.2", {"start": v(12.4, -32) * mm, "end": v(-12.6, -32) * mm});
            skLineSegment(sketch, "E41.2.3", {"start": v(-12.6, -36.5) * mm, "end": v(-12.6, -32) * mm});
            skLineSegment(sketch, "E41.3.0", {"start": v(36.5, 12.4) * mm, "end": v(36.5, -12.6) * mm});
            skLineSegment(sketch, "E41.3.1", {"start": v(36.5, 12.4) * mm, "end": v(32, 12.4) * mm});
            skLineSegment(sketch, "E41.3.2", {"start": v(32, 12.4) * mm, "end": v(32, -12.6) * mm});
            skLineSegment(sketch, "E41.3.3", {"start": v(36.5, -12.6) * mm, "end": v(32, -12.6) * mm});
            skPoint(sketch, "E41.center", {"position": v(0, 0) * mm});
            skSolve(sketch);
        }
        {
            var Q0;
            Q0 = qSketchRegion(id + "F44", true);
            extrude(context, id + "F45", {"entities" : qUnion([Q0]), "operationType" : NewBodyOperationType.ADD, "depth" : 5 * mm});
        }
        {
            var Q0;
            Q0=makeQuery(id+"F15.opExtrude","CAP_FACE",FACE,{"disambiguationData":[OSD([sQuery(id+"F14.wireOp",EDGE,"E7.0"),sQuery(id+"F14.wireOp",EDGE,"E7.1"),sQuery(id+"F14.wireOp",EDGE,"E7.2"),sQuery(id+"F14.wireOp",EDGE,"E7.3")])],"isStart":false});
            var sketch = newSketch(context, id + "F46", { "sketchPlane" : qUnion([Q0])});
            skLineSegment(sketch, "E42.bottom", {"start": v(-12.39, 32) * mm, "end": v(12.61, 32) * mm});
            skLineSegment(sketch, "E42.top", {"start": v(-12.39, 27.5) * mm, "end": v(12.61, 27.5) * mm});
            skLineSegment(sketch, "E42.left", {"start": v(-12.39, 32) * mm, "end": v(-12.39, 27.5) * mm});
            skLineSegment(sketch, "E42.right", {"start": v(12.61, 32) * mm, "end": v(12.61, 27.5) * mm});
            skLineSegment(sketch, "E43.1.0", {"start": v(-32, -12.39) * mm, "end": v(-32, 12.61) * mm});
            skLineSegment(sketch, "E43.1.1", {"start": v(-32, -12.39) * mm, "end": v(-27.5, -12.39) * mm});
            skLineSegment(sketch, "E43.1.2", {"start": v(-27.5, -12.39) * mm, "end": v(-27.5, 12.61) * mm});
            skLineSegment(sketch, "E43.1.3", {"start": v(-32, 12.61) * mm, "end": v(-27.5, 12.61) * mm});
            skLineSegment(sketch, "E43.2.0", {"start": v(12.39, -32) * mm, "end": v(-12.61, -32) * mm});
            skLineSegment(sketch, "E43.2.1", {"start": v(12.39, -32) * mm, "end": v(12.39, -27.5) * mm});
            skLineSegment(sketch, "E43.2.2", {"start": v(12.39, -27.5) * mm, "end": v(-12.61, -27.5) * mm});
            skLineSegment(sketch, "E43.2.3", {"start": v(-12.61, -32) * mm, "end": v(-12.61, -27.5) * mm});
            skLineSegment(sketch, "E43.3.0", {"start": v(32, 12.39) * mm, "end": v(32, -12.61) * mm});
            skLineSegment(sketch, "E43.3.1", {"start": v(32, 12.39) * mm, "end": v(27.5, 12.39) * mm});
            skLineSegment(sketch, "E43.3.2", {"start": v(27.5, 12.39) * mm, "end": v(27.5, -12.61) * mm});
            skLineSegment(sketch, "E43.3.3", {"start": v(32, -12.61) * mm, "end": v(27.5, -12.61) * mm});
            skPoint(sketch, "E43.center", {"position": v(0, 0) * mm});
            skSolve(sketch);
        }
        {
            var Q0;
            Q0 = qSketchRegion(id + "F46", true);
            extrude(context, id + "F47", {"entities" : qUnion([Q0]), "operationType" : NewBodyOperationType.ADD, "depth" : 5 * mm});
        }
        {
            var Q0;
            Q0=makeQuery(id+"F18.imprint","IMPRINT",FACE,{"disambiguationData":[TD([[makeQuery(id+"F18.imprint","IMPRINT",EDGE,{"derivedFrom":sQuery(id+"F18.wireOp",EDGE,"E9.0")}),-1.0]])]});
            var sketch = newSketch(context, id + "F48", { "sketchPlane" : qUnion([Q0])});
            skLineSegment(sketch, "E44.bottom", {"start": v(-12.5, 27.52) * mm, "end": v(12.5, 27.52) * mm});
            skLineSegment(sketch, "E44.top", {"start": v(-12.5, 23.02) * mm, "end": v(12.5, 23.02) * mm});
            skLineSegment(sketch, "E44.left", {"start": v(-12.5, 27.52) * mm, "end": v(-12.5, 23.02) * mm});
            skLineSegment(sketch, "E44.right", {"start": v(12.5, 27.52) * mm, "end": v(12.5, 23.02) * mm});
            skLineSegment(sketch, "E45.1.0", {"start": v(-23.02, -12.5) * mm, "end": v(-23.02, 12.5) * mm});
            skLineSegment(sketch, "E45.1.1", {"start": v(-27.52, -12.5) * mm, "end": v(-23.02, -12.5) * mm});
            skLineSegment(sketch, "E45.1.2", {"start": v(-27.52, -12.5) * mm, "end": v(-27.52, 12.5) * mm});
            skLineSegment(sketch, "E45.1.3", {"start": v(-27.52, 12.5) * mm, "end": v(-23.02, 12.5) * mm});
            skLineSegment(sketch, "E45.2.0", {"start": v(12.5, -23.02) * mm, "end": v(-12.5, -23.02) * mm});
            skLineSegment(sketch, "E45.2.1", {"start": v(12.5, -27.52) * mm, "end": v(12.5, -23.02) * mm});
            skLineSegment(sketch, "E45.2.2", {"start": v(12.5, -27.52) * mm, "end": v(-12.5, -27.52) * mm});
            skLineSegment(sketch, "E45.2.3", {"start": v(-12.5, -27.52) * mm, "end": v(-12.5, -23.02) * mm});
            skLineSegment(sketch, "E45.3.0", {"start": v(23.02, 12.5) * mm, "end": v(23.02, -12.5) * mm});
            skLineSegment(sketch, "E45.3.1", {"start": v(27.52, 12.5) * mm, "end": v(23.02, 12.5) * mm});
            skLineSegment(sketch, "E45.3.2", {"start": v(27.52, 12.5) * mm, "end": v(27.52, -12.5) * mm});
            skLineSegment(sketch, "E45.3.3", {"start": v(27.52, -12.5) * mm, "end": v(23.02, -12.5) * mm});
            skPoint(sketch, "E45.center", {"position": v(0, 0) * mm});
            skLineSegment(sketch, "E46", {"start": v(-12.5, -50) * mm, "end": v(-12.5, 49.97) * mm, "construction": true});
            skSolve(sketch);
        }
        {
            var Q0;
            Q0 = qSketchRegion(id + "F48", true);
            extrude(context, id + "F49", {"entities" : qUnion([Q0]), "operationType" : NewBodyOperationType.ADD, "depth" : 5 * mm});
        }
        {
            var Q0;
            Q0=makeQuery(id+"F20.opExtrude","CAP_FACE",FACE,{"disambiguationData":[OSD([sQuery(id+"F19.wireOp",EDGE,"E11.bottom"),sQuery(id+"F19.wireOp",EDGE,"E11.top"),sQuery(id+"F19.wireOp",EDGE,"E11.left"),sQuery(id+"F19.wireOp",EDGE,"E11.right")])],"isStart":false});
            var sketch = newSketch(context, id + "F50", { "sketchPlane" : qUnion([Q0])});
            skLineSegment(sketch, "E47.bottom", {"start": v(-12.5, 23) * mm, "end": v(12.5, 23) * mm});
            skLineSegment(sketch, "E47.top", {"start": v(-12.5, 18.5) * mm, "end": v(12.5, 18.5) * mm});
            skLineSegment(sketch, "E47.left", {"start": v(-12.5, 23) * mm, "end": v(-12.5, 18.5) * mm});
            skLineSegment(sketch, "E47.right", {"start": v(12.5, 23) * mm, "end": v(12.5, 18.5) * mm});
            skLineSegment(sketch, "E48.1.0", {"start": v(-23, -12.5) * mm, "end": v(-18.5, -12.5) * mm});
            skLineSegment(sketch, "E48.1.1", {"start": v(-18.5, -12.5) * mm, "end": v(-18.5, 12.5) * mm});
            skLineSegment(sketch, "E48.1.2", {"start": v(-23, -12.5) * mm, "end": v(-23, 12.5) * mm});
            skLineSegment(sketch, "E48.1.3", {"start": v(-23, 12.5) * mm, "end": v(-18.5, 12.5) * mm});
            skLineSegment(sketch, "E48.2.0", {"start": v(12.5, -23) * mm, "end": v(12.5, -18.5) * mm});
            skLineSegment(sketch, "E48.2.1", {"start": v(12.5, -18.5) * mm, "end": v(-12.5, -18.5) * mm});
            skLineSegment(sketch, "E48.2.2", {"start": v(12.5, -23) * mm, "end": v(-12.5, -23) * mm});
            skLineSegment(sketch, "E48.2.3", {"start": v(-12.5, -23) * mm, "end": v(-12.5, -18.5) * mm});
            skLineSegment(sketch, "E48.3.0", {"start": v(23, 12.5) * mm, "end": v(18.5, 12.5) * mm});
            skLineSegment(sketch, "E48.3.1", {"start": v(18.5, 12.5) * mm, "end": v(18.5, -12.5) * mm});
            skLineSegment(sketch, "E48.3.2", {"start": v(23, 12.5) * mm, "end": v(23, -12.5) * mm});
            skLineSegment(sketch, "E48.3.3", {"start": v(23, -12.5) * mm, "end": v(18.5, -12.5) * mm});
            skPoint(sketch, "E48.center", {"position": v(0, 0) * mm});
            skSolve(sketch);
        }
        {
            var Q0;
            Q0 = qSketchRegion(id + "F50", true);
            extrude(context, id + "F51", {"entities" : qUnion([Q0]), "operationType" : NewBodyOperationType.ADD, "depth" : 5 * mm});
        }
        {
            var Q0;
            Q0=makeQuery(id+"F22.opExtrude","CAP_FACE",FACE,{"disambiguationData":[OSD([sQuery(id+"F21.wireOp",EDGE,"E12.bottom"),sQuery(id+"F21.wireOp",EDGE,"E12.top"),sQuery(id+"F21.wireOp",EDGE,"E12.left"),sQuery(id+"F21.wireOp",EDGE,"E12.right")])],"isStart":false});
            var sketch = newSketch(context, id + "F52", { "sketchPlane" : qUnion([Q0])});
            skLineSegment(sketch, "E49.bottom", {"start": v(-12.54, 18.5) * mm, "end": v(12.46, 18.5) * mm});
            skLineSegment(sketch, "E49.top", {"start": v(-12.54, 8.5) * mm, "end": v(12.46, 8.5) * mm});
            skLineSegment(sketch, "E49.left", {"start": v(-12.54, 18.5) * mm, "end": v(-12.54, 8.5) * mm});
            skLineSegment(sketch, "E49.right", {"start": v(12.46, 18.5) * mm, "end": v(12.46, 8.5) * mm});
            skLineSegment(sketch, "E50.1.0", {"start": v(-18.5, -12.54) * mm, "end": v(-8.5, -12.54) * mm});
            skLineSegment(sketch, "E50.1.1", {"start": v(-18.5, -12.54) * mm, "end": v(-18.5, 12.46) * mm});
            skLineSegment(sketch, "E50.1.2", {"start": v(-18.5, 12.46) * mm, "end": v(-8.5, 12.46) * mm});
            skLineSegment(sketch, "E50.1.3", {"start": v(-8.5, -12.54) * mm, "end": v(-8.5, 12.46) * mm});
            skLineSegment(sketch, "E50.2.0", {"start": v(12.54, -18.5) * mm, "end": v(12.54, -8.5) * mm});
            skLineSegment(sketch, "E50.2.1", {"start": v(12.54, -18.5) * mm, "end": v(-12.46, -18.5) * mm});
            skLineSegment(sketch, "E50.2.2", {"start": v(-12.46, -18.5) * mm, "end": v(-12.46, -8.5) * mm});
            skLineSegment(sketch, "E50.2.3", {"start": v(12.54, -8.5) * mm, "end": v(-12.46, -8.5) * mm});
            skLineSegment(sketch, "E50.3.0", {"start": v(18.5, 12.54) * mm, "end": v(8.5, 12.54) * mm});
            skLineSegment(sketch, "E50.3.1", {"start": v(18.5, 12.54) * mm, "end": v(18.5, -12.46) * mm});
            skLineSegment(sketch, "E50.3.2", {"start": v(18.5, -12.46) * mm, "end": v(8.5, -12.46) * mm});
            skLineSegment(sketch, "E50.3.3", {"start": v(8.5, 12.54) * mm, "end": v(8.5, -12.46) * mm});
            skPoint(sketch, "E50.center", {"position": v(0, 0) * mm});
            skSolve(sketch);
        }
        {
            var Q0;
            Q0 = qSketchRegion(id + "F52", true);
            extrude(context, id + "F53", {"entities" : qUnion([Q0]), "operationType" : NewBodyOperationType.ADD, "depth" : 5 * mm});
        }
        {
            var Q0;
            Q0=makeQuery(id+"F24.opExtrude","CAP_FACE",FACE,{"disambiguationData":[OSD([sQuery(id+"F23.wireOp",EDGE,"E13.bottom"),sQuery(id+"F23.wireOp",EDGE,"E13.top"),sQuery(id+"F23.wireOp",EDGE,"E13.left"),sQuery(id+"F23.wireOp",EDGE,"E13.right")])],"isStart":false});
            var sketch = newSketch(context, id + "F54", { "sketchPlane" : qUnion([Q0])});
            skLineSegment(sketch, "E51.bottom", {"start": v(-9.05, 14) * mm, "end": v(8.95, 14) * mm});
            skLineSegment(sketch, "E51.top", {"start": v(-9.05, 4) * mm, "end": v(8.95, 4) * mm});
            skLineSegment(sketch, "E51.left", {"start": v(-9.05, 14) * mm, "end": v(-9.05, 4) * mm});
            skLineSegment(sketch, "E51.right", {"start": v(8.95, 14) * mm, "end": v(8.95, 4) * mm});
            skPoint(sketch, "E52.center", {"position": v(-0.87, 0.07) * mm});
            skLineSegment(sketch, "E53.bottom", {"start": v(-9.07, -14) * mm, "end": v(8.93, -14) * mm});
            skLineSegment(sketch, "E53.top", {"start": v(-9.07, -4) * mm, "end": v(8.93, -4) * mm});
            skLineSegment(sketch, "E53.left", {"start": v(-9.07, -14) * mm, "end": v(-9.07, -4) * mm});
            skLineSegment(sketch, "E53.right", {"start": v(8.93, -14) * mm, "end": v(8.93, -4) * mm});
            skLineSegment(sketch, "E54.bottom", {"start": v(14.3, 8.88) * mm, "end": v(4.3, 8.88) * mm});
            skLineSegment(sketch, "E54.top", {"start": v(14.3, -9.12) * mm, "end": v(4.3, -9.12) * mm});
            skLineSegment(sketch, "E54.left", {"start": v(14.3, 8.88) * mm, "end": v(14.3, -9.12) * mm});
            skLineSegment(sketch, "E54.right", {"start": v(4.3, 8.88) * mm, "end": v(4.3, -9.12) * mm});
            skLineSegment(sketch, "E55.bottom", {"start": v(-13.7, 9.1) * mm, "end": v(-9.5, 9.1) * mm});
            skLineSegment(sketch, "E55.top", {"start": v(-13.7, -8.9) * mm, "end": v(-9.5, -8.9) * mm});
            skLineSegment(sketch, "E55.left", {"start": v(-13.7, 9.1) * mm, "end": v(-13.7, -8.9) * mm});
            skLineSegment(sketch, "E55.right", {"start": v(-9.5, 9.1) * mm, "end": v(-9.5, -8.9) * mm});
            skSolve(sketch);
        }
        {
            var Q0;
            Q0 = qSketchRegion(id + "F54", true);
            extrude(context, id + "F55", {"entities" : qUnion([Q0]), "operationType" : NewBodyOperationType.ADD, "depth" : 5 * mm});
        }
    });
